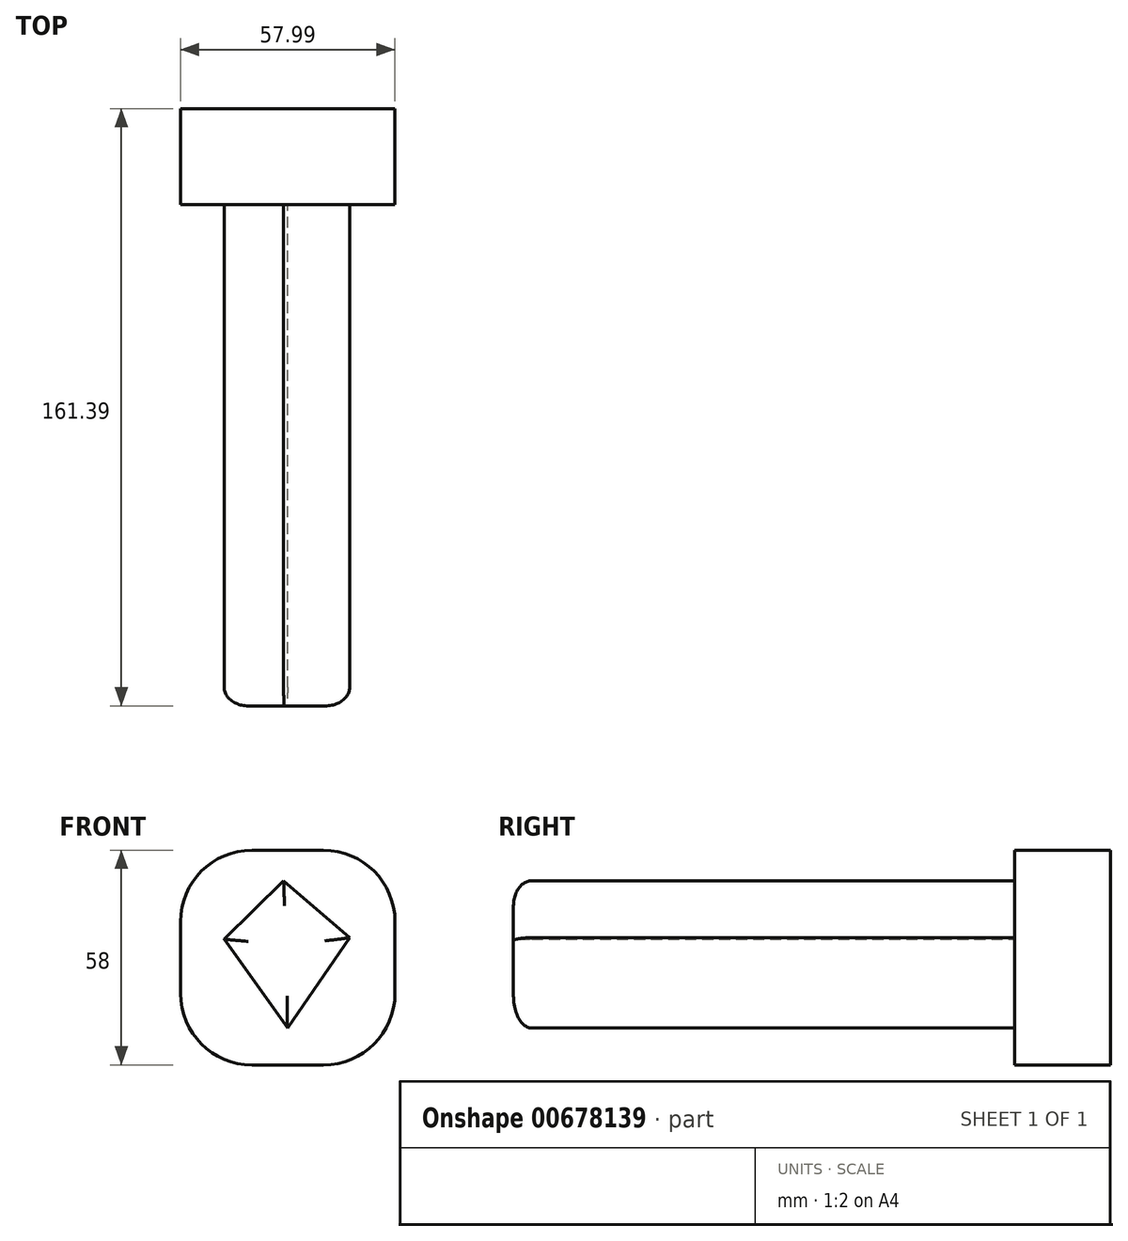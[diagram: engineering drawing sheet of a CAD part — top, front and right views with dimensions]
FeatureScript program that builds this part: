
annotation { "Feature Type Name" : "Feature", "Feature Type Description" : "" }
export const myFeature = defineFeature(function(context is Context, id is Id, definition is map)
    precondition{}
    {
        {
            var Q0;
            Q0=qCreatedBy(makeId("Front.planeOp"),FACE);
            var sketch = newSketch(context, id + "F0", { "sketchPlane" : qUnion([Q0])});
            skLineSegment(sketch, "E0", {"start": v(0.33, -22.07) * mm, "end": v(-16.77, 1.93) * mm});
            skLineSegment(sketch, "E1", {"start": v(-16.77, 1.93) * mm, "end": v(-0.7, 17.78) * mm});
            skLineSegment(sketch, "E2", {"start": v(-0.7, 17.78) * mm, "end": v(17.15, 2.36) * mm});
            skLineSegment(sketch, "E3", {"start": v(17.15, 2.36) * mm, "end": v(0.33, -22.07) * mm});
            skSolve(sketch);
        }
        {
            var Q0;
            Q0=makeQuery(id+"F0.imprint","IMPRINT",FACE,{"disambiguationData":[TD([[makeQuery(id+"F0.imprint","IMPRINT",EDGE,{"derivedFrom":sQuery(id+"F0.wireOp",EDGE,"E0")}),-1.0]])]});
            var Q1;
            Q1=sQuery(id+"F0.wireOp",EDGE,"E0");
            var Q2;
            Q2=sQuery(id+"F0.wireOp",EDGE,"E1");
            var Q3;
            Q3=sQuery(id+"F0.wireOp",EDGE,"E2");
            var Q4;
            Q4=sQuery(id+"F0.wireOp",EDGE,"E3");
            extrude(context, id + "F1", {"entities" : qUnion([Q0]), "surfaceEntities" : qUnion([Q1, Q2, Q3, Q4]), "depth" : 150 * mm, "offsetDistance" : 25 * mm});
        }
        {
            var Q0;
            Q0=qCreatedBy(makeId("Top.planeOp"),FACE);
            var sketch = newSketch(context, id + "F2", { "sketchPlane" : qUnion([Q0])});
            skLineSegment(sketch, "E4.bottom", {"start": v(-28.59, 11.39) * mm, "end": v(29.4, 11.39) * mm});
            skLineSegment(sketch, "E4.top", {"start": v(-28.59, -14.48) * mm, "end": v(29.4, -14.48) * mm});
            skLineSegment(sketch, "E4.left", {"start": v(-28.59, 11.39) * mm, "end": v(-28.59, -14.48) * mm});
            skLineSegment(sketch, "E4.right", {"start": v(29.4, 11.39) * mm, "end": v(29.4, -14.48) * mm});
            skSolve(sketch);
        }
        {
            var Q0;
            Q0=makeQuery(id+"F2.imprint","IMPRINT",FACE,{"disambiguationData":[TD([[makeQuery(id+"F2.imprint","IMPRINT",EDGE,{"derivedFrom":sQuery(id+"F2.wireOp",EDGE,"E4.bottom")}),-1.0]])]});
            extrude(context, id + "F3", {"entities" : qUnion([Q0]), "operationType" : NewBodyOperationType.ADD, "depth" : 26 * mm, "offsetDistance" : 25 * mm, "hasSecondDirection" : true, "secondDirectionOppositeDirection" : true, "secondDirectionDepth" : 32 * mm});
        }
        {
            var Q0;
            Q0=makeQuery(id+"F3.opExtrude","CAP_EDGE",EDGE,{"disambiguationData":[OSD([sQuery(id+"F2.wireOp",EDGE,"E4.left")])],"isStart":true});
            var Q1;
            Q1=makeQuery(id+"F3.opExtrude","CAP_EDGE",EDGE,{"disambiguationData":[OSD([sQuery(id+"F2.wireOp",EDGE,"E4.right")])],"isStart":true});
            var Q2;
            Q2=makeQuery(id+"F3.opExtrude","CAP_EDGE",EDGE,{"disambiguationData":[OSD([sQuery(id+"F2.wireOp",EDGE,"E4.right")])],"isStart":false});
            var Q3;
            Q3=makeQuery(id+"F3.opExtrude","CAP_EDGE",EDGE,{"disambiguationData":[OSD([sQuery(id+"F2.wireOp",EDGE,"E4.left")])],"isStart":false});
            fillet(context, id + "F4", {"entities" : qUnion([Q0, Q1, Q2, Q3]), "radius" : 19.3 * mm, "tangentPropagation" : true, "allowEdgeOverflow" : false});
        }
        {
            var Q0;
            Q0=makeQuery(id+"F1.opExtrude","CAP_EDGE",EDGE,{"disambiguationData":[OSD([sQuery(id+"F0.wireOp",EDGE,"E2")])],"isStart":false});
            var Q1;
            Q1=makeQuery(id+"F1.opExtrude","CAP_EDGE",EDGE,{"disambiguationData":[OSD([sQuery(id+"F0.wireOp",EDGE,"E3")])],"isStart":false});
            var Q2;
            Q2=makeQuery(id+"F1.opExtrude","CAP_EDGE",EDGE,{"disambiguationData":[OSD([sQuery(id+"F0.wireOp",EDGE,"E1")])],"isStart":false});
            var Q3;
            Q3=makeQuery(id+"F1.opExtrude","CAP_EDGE",EDGE,{"disambiguationData":[OSD([sQuery(id+"F0.wireOp",EDGE,"E0")])],"isStart":false});
            fillet(context, id + "F5", {"entities" : qUnion([Q0, Q1, Q2, Q3]), "radius" : 5 * mm, "tangentPropagation" : true, "allowEdgeOverflow" : false});
        }
    });
